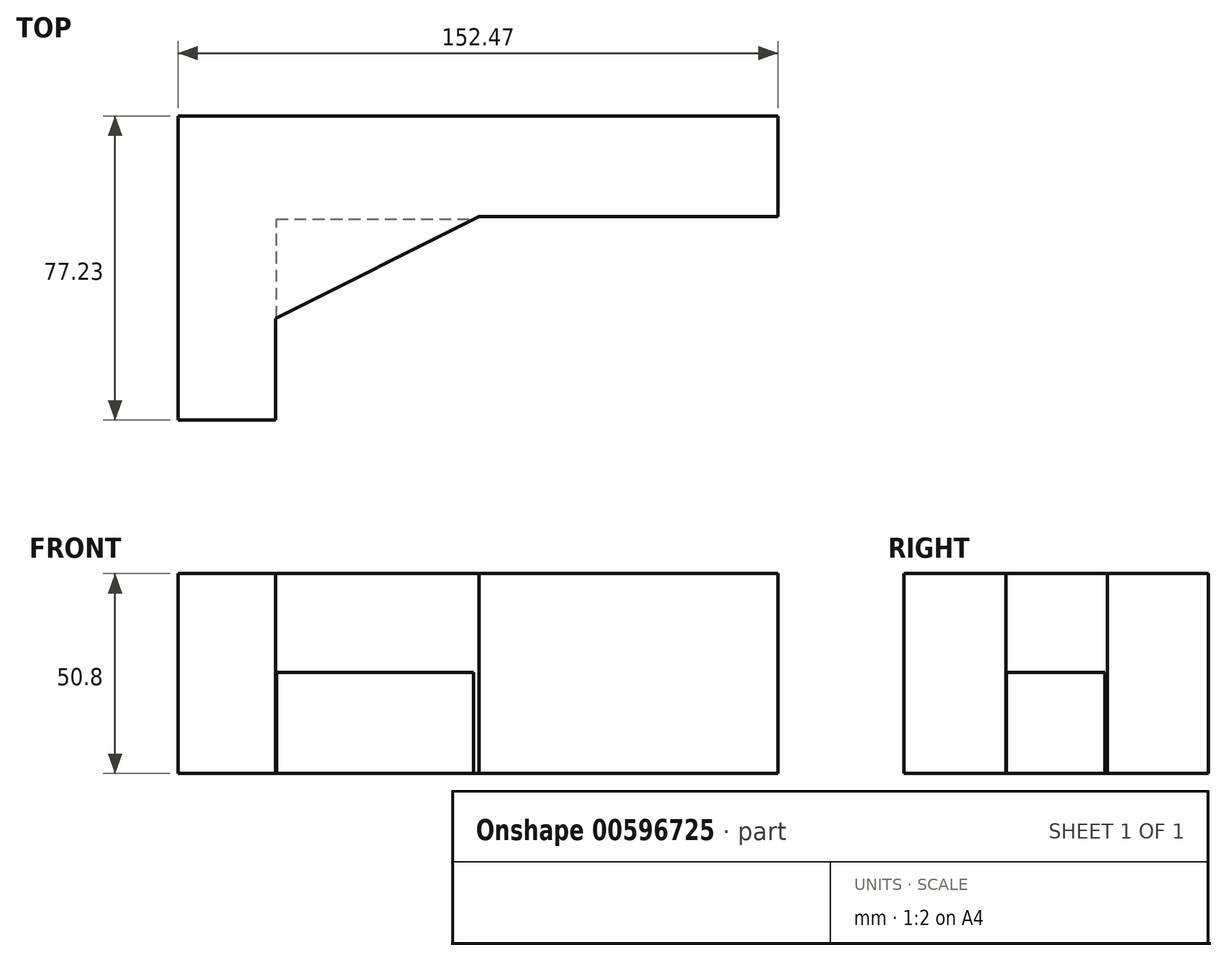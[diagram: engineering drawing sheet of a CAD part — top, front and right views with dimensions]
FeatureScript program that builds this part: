
annotation { "Feature Type Name" : "Feature", "Feature Type Description" : "" }
export const myFeature = defineFeature(function(context is Context, id is Id, definition is map)
    precondition{}
    {
        {
            var Q0;
            Q0=qCreatedBy(makeId("Top.planeOp"),FACE);
            var sketch = newSketch(context, id + "F0", { "sketchPlane" : qUnion([Q0])});
            skLineSegment(sketch, "E0", {"start": v(0, 0) * mm, "end": v(0, 77.23) * mm});
            skLineSegment(sketch, "E1", {"start": v(0, 77.23) * mm, "end": v(152.47, 77.23) * mm});
            skLineSegment(sketch, "E2", {"start": v(152.47, 77.23) * mm, "end": v(152.47, 51.68) * mm});
            skLineSegment(sketch, "E3", {"start": v(152.47, 51.68) * mm, "end": v(76.45, 51.68) * mm});
            skLineSegment(sketch, "E4", {"start": v(76.45, 51.68) * mm, "end": v(24.72, 51.68) * mm});
            skLineSegment(sketch, "E5", {"start": v(24.72, 51.68) * mm, "end": v(24.72, 0) * mm});
            skLineSegment(sketch, "E6", {"start": v(24.72, 0) * mm, "end": v(0, 0) * mm});
            skLineSegment(sketch, "E7", {"start": v(76.45, 51.68) * mm, "end": v(24.72, 25.84) * mm});
            skSolve(sketch);
        }
        {
            var Q0;
            Q0 = qSketchRegion(id + "F0", true);
            extrude(context, id + "F1", {"entities" : qUnion([Q0]), "depth" : 50.8 * mm, "offsetDistance" : 25.4 * mm});
        }
        {
            var Q0;
            Q0=qCreatedBy(makeId("Top.planeOp"),FACE);
            var sketch = newSketch(context, id + "F2", { "sketchPlane" : qUnion([Q0])});
            skLineSegment(sketch, "E8", {"start": v(24.97, 24.17) * mm, "end": v(24.97, 51.02) * mm});
            skLineSegment(sketch, "E9", {"start": v(24.97, 51.02) * mm, "end": v(77.13, 51.02) * mm});
            skLineSegment(sketch, "E10", {"start": v(77.13, 51.02) * mm, "end": v(24.97, 24.17) * mm});
            skSolve(sketch);
        }
        {
            var Q0;
            Q0 = qSketchRegion(id + "F2", true);
            extrude(context, id + "F3", {"entities" : qUnion([Q0]), "operationType" : NewBodyOperationType.REMOVE, "depth" : 25.65 * mm, "offsetDistance" : 25.4 * mm});
        }
    });
